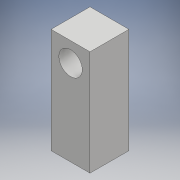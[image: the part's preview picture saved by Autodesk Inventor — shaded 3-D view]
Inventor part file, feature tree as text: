
AUTODESK INVENTOR PART (.ipt)
format: ipt  version: 2018 (Build 220112000, 112)  size: 232,448 bytes
history: native  units: mm
features: extrude x3, sketch x3
ambient origin geometry x8: Origin, YZ Plane, XZ Plane, XY Plane, X Axis, Y Axis, Z Axis, Center Point
bodies: Solid1 (feature_tree)
feature tree (6):
  extrude  "Extrusion1"  Depth=27.0mm
  extrude  "Extrusion2"  Depth=10.0mm
  extrude  "Extrusion3"  Depth=10.0mm TaperAngle=0.0deg
  sketch  "Sketch1"  dims[d0=10.0mm d1=27.0mm]
  sketch  "Sketch2"  dims[d2=10.0mm d3=0.0mm d4=5.0mm]
  sketch  "Sketch3"  dims[d5=6.0mm d6=10.0mm d7=0.0mm d8=5.0mm d9=5.0mm d10=3.9mm d11=15.0mm d12=0.0mm]
